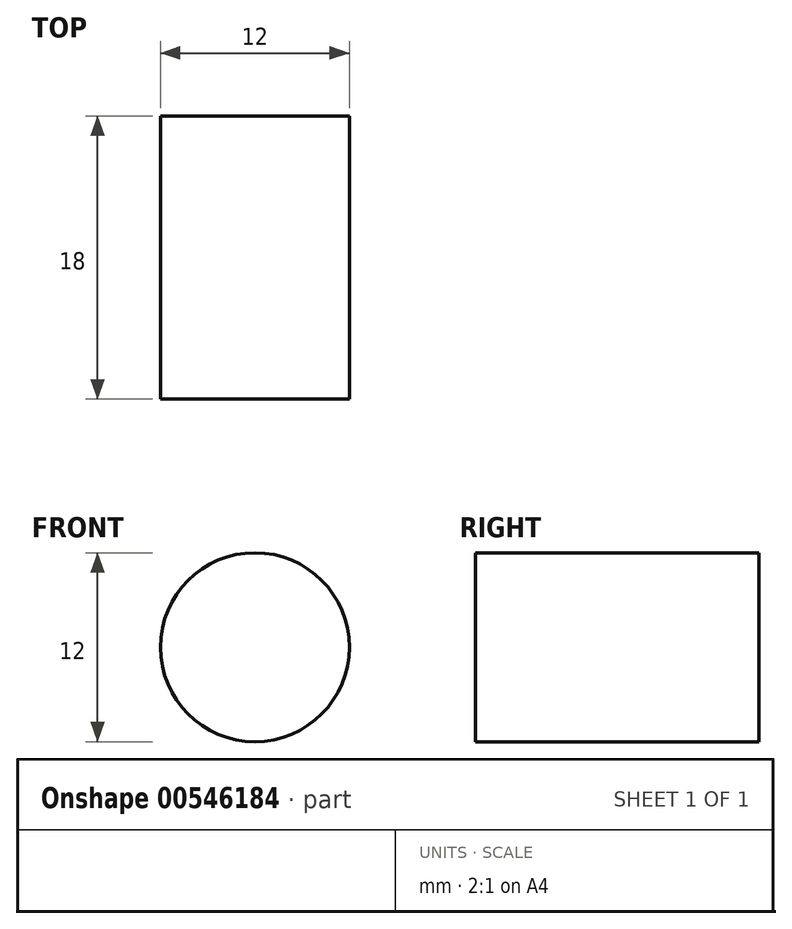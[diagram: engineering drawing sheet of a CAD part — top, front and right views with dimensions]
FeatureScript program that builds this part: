
annotation { "Feature Type Name" : "Feature", "Feature Type Description" : "" }
export const myFeature = defineFeature(function(context is Context, id is Id, definition is map)
    precondition{}
    {
        {
            var Q0;
            Q0=qCreatedBy(makeId("Front.planeOp"),FACE);
            var sketch = newSketch(context, id + "F0", { "sketchPlane" : qUnion([Q0])});
            skCircle(sketch, "E0", {"center": v(0, 0) * mm, "radius": 6 * mm});
            skSolve(sketch);
        }
        {
            var Q0;
            Q0 = qSketchRegion(id + "F0", true);
            extrude(context, id + "F1", {"entities" : qUnion([Q0]), "depth" : 18 * mm, "offsetDistance" : 25 * mm});
        }
    });
